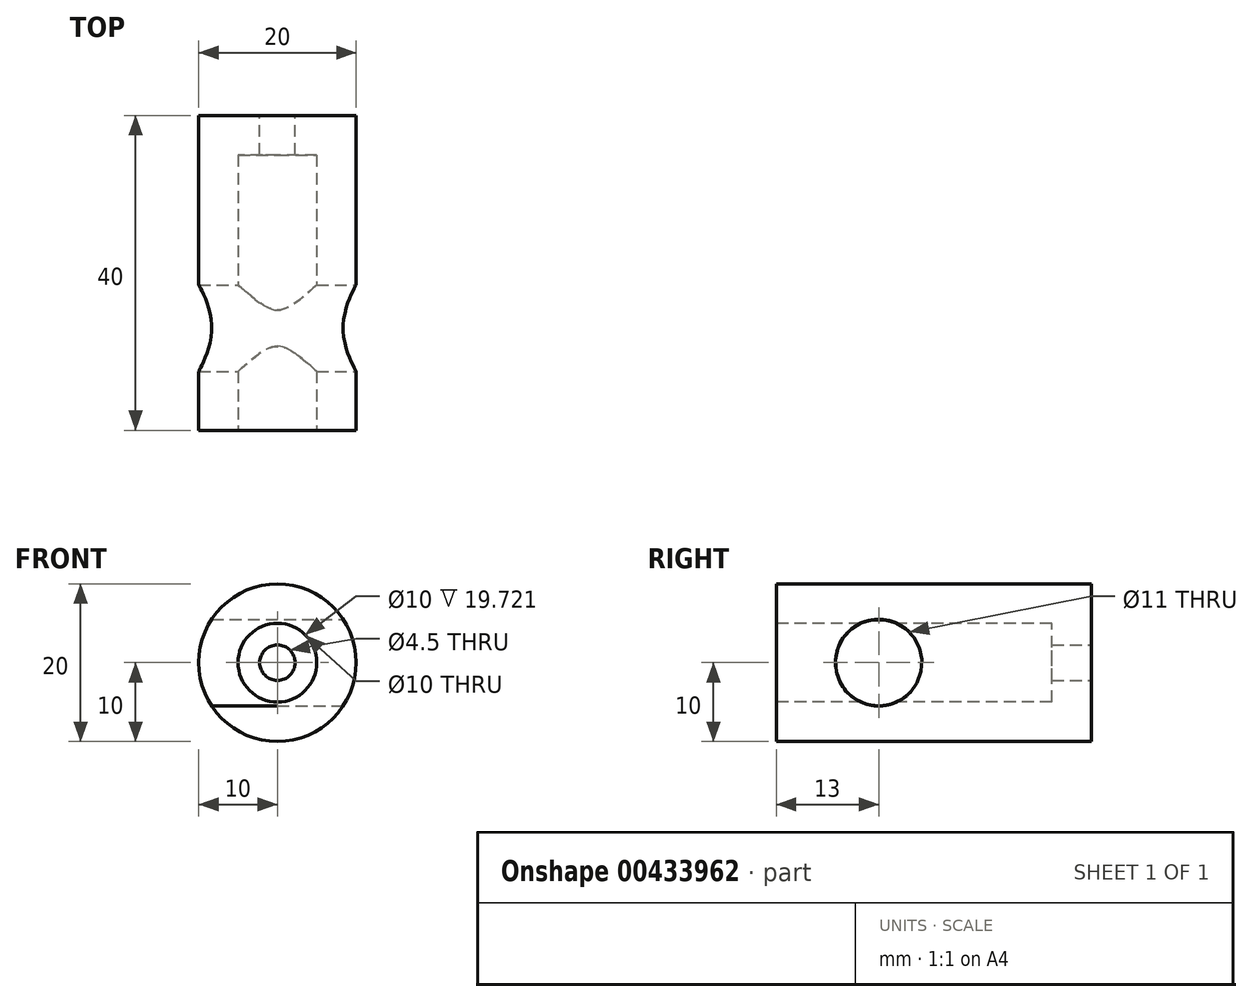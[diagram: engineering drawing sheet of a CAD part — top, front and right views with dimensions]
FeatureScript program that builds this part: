
annotation { "Feature Type Name" : "Feature", "Feature Type Description" : "" }
export const myFeature = defineFeature(function(context is Context, id is Id, definition is map)
    precondition{}
    {
        {
            var Q0;
            Q0=qCreatedBy(makeId("Front.planeOp"),FACE);
            var sketch = newSketch(context, id + "F0", { "sketchPlane" : qUnion([Q0])});
            skCircle(sketch, "E0", {"center": v(0, 0) * mm, "radius": 10 * mm});
            skSolve(sketch);
        }
        {
            var Q0;
            Q0 = qSketchRegion(id + "F0", true);
            extrude(context, id + "F1", {"entities" : qUnion([Q0]), "depth" : 40 * mm});
        }
        {
            var Q0;
            Q0=makeQuery(id+"F1.opExtrude","CAP_FACE",FACE,{"disambiguationData":[OSD([sQuery(id+"F0.wireOp",EDGE,"E0")])],"isStart":true});
            var sketch = newSketch(context, id + "F2", { "sketchPlane" : qUnion([Q0])});
            skCircle(sketch, "E1", {"center": v(0, 0) * mm, "radius": 2.25 * mm});
            skSolve(sketch);
        }
        {
            var Q0;
            Q0 = qSketchRegion(id + "F2", true);
            extrude(context, id + "F3", {"entities" : qUnion([Q0]), "operationType" : NewBodyOperationType.REMOVE, "endBound" : BoundingType.UP_TO_NEXT, "oppositeDirection" : true, "depth" : 25 * mm});
        }
        {
            var Q0;
            Q0=makeQuery(id+"F1.opExtrude","CAP_FACE",FACE,{"disambiguationData":[OSD([sQuery(id+"F0.wireOp",EDGE,"E0")])],"isStart":false});
            var sketch = newSketch(context, id + "F4", { "sketchPlane" : qUnion([Q0])});
            skCircle(sketch, "E2", {"center": v(0, 0) * mm, "radius": 5 * mm});
            skSolve(sketch);
        }
        {
            var Q0;
            Q0 = qSketchRegion(id + "F4", true);
            extrude(context, id + "F5", {"entities" : qUnion([Q0]), "operationType" : NewBodyOperationType.REMOVE, "oppositeDirection" : true, "depth" : 35 * mm});
        }
        {
            var Q0;
            Q0=qCreatedBy(makeId("Right.planeOp"),FACE);
            var sketch = newSketch(context, id + "F6", { "sketchPlane" : qUnion([Q0])});
            skCircle(sketch, "E3", {"center": v(-27, 0) * mm, "radius": 5.5 * mm});
            skSolve(sketch);
        }
        {
            var Q0;
            Q0 = qSketchRegion(id + "F6", true);
            extrude(context, id + "F7", {"entities" : qUnion([Q0]), "operationType" : NewBodyOperationType.REMOVE, "endBound" : BoundingType.THROUGH_ALL, "oppositeDirection" : true, "depth" : 25 * mm, "hasSecondDirection" : true, "secondDirectionBound" : SecondDirectionBoundingType.THROUGH_ALL, "secondDirectionOppositeDirection" : false, "secondDirectionDepth" : 25 * mm});
        }
    });
